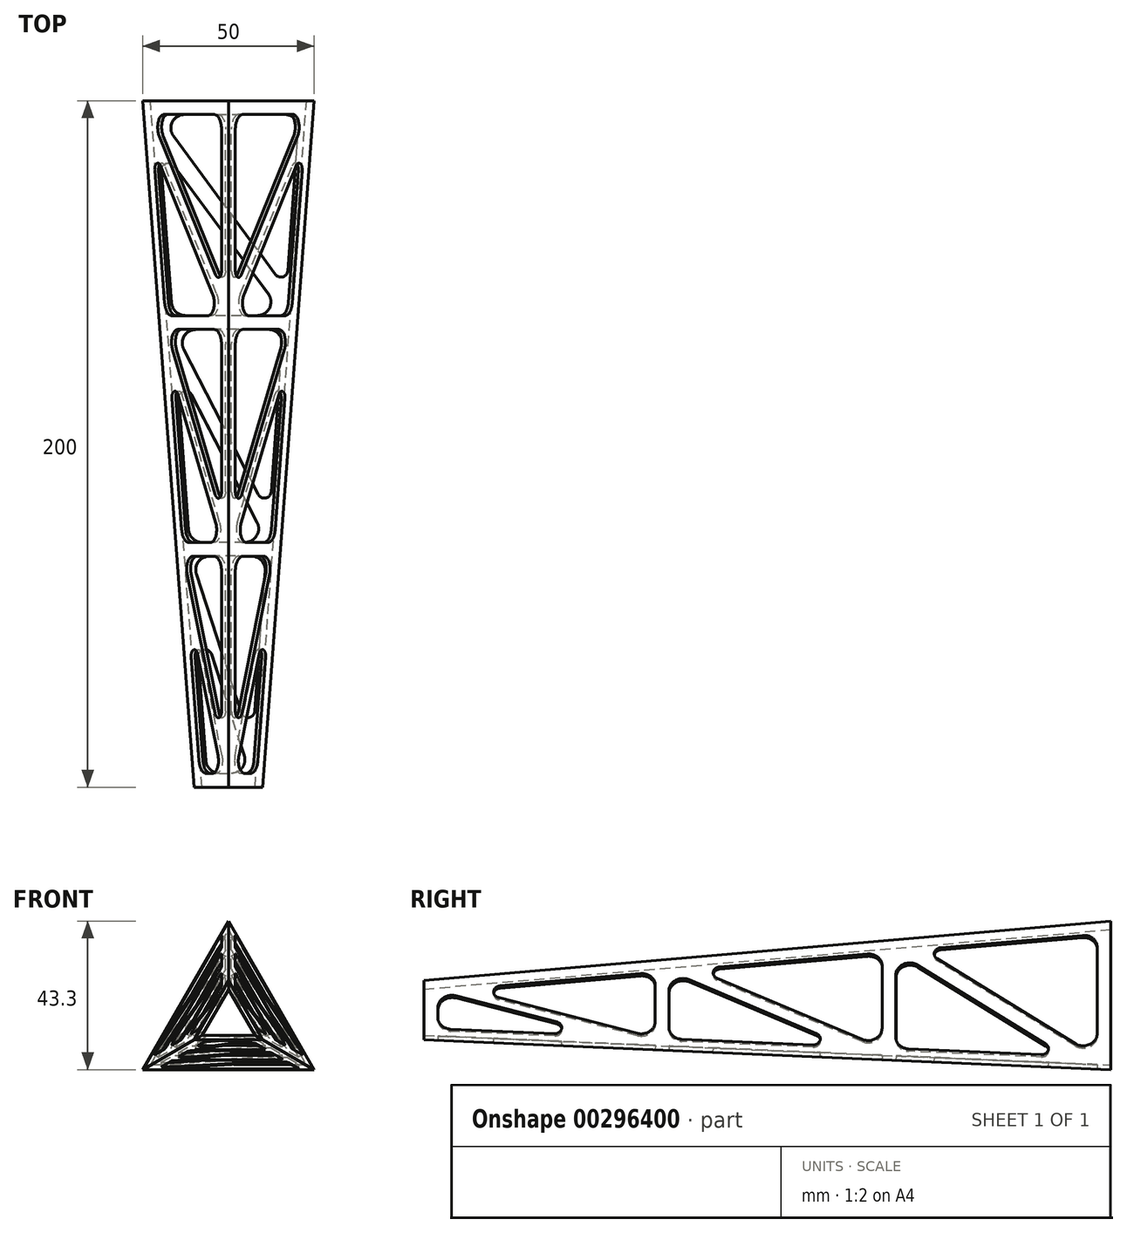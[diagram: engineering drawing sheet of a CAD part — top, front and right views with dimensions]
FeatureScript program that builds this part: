
annotation { "Feature Type Name" : "Feature", "Feature Type Description" : "" }
export const myFeature = defineFeature(function(context is Context, id is Id, definition is map)
    precondition{}
    {
        {
            assignVariable(context, id + "F0", {"name" : "thick", "anyValue" : 4});
        }
        {
            assignVariable(context, id + "F1", {"name" : "thinBy", "anyValue" : 1});
        }
        {
            assignVariable(context, id + "F2", {"name" : "length", "anyValue" : 200});
        }
        {
            assignVariable(context, id + "F3", {"name" : "rad", "anyValue" : 4});
        }
        {
            assignVariable(context, id + "F4", {"name" : "radSmall", "anyValue" : 2});
        }
        {
            var Q0;
            Q0=qCreatedBy(makeId("Right.planeOp"),FACE);
            var sketch = newSketch(context, id + "F5", { "sketchPlane" : qUnion([Q0])});
            skLineSegment(sketch, "E0", {"start": v(0, 0) * mm, "end": v(-200, 0) * mm, "construction": true});
            skSolve(sketch);
        }
        {
            var Q0;
            Q0=qCreatedBy(makeId("Front.planeOp"),FACE);
            var sketch = newSketch(context, id + "F6", { "sketchPlane" : qUnion([Q0])});
            skLineSegment(sketch, "E1", {"start": v(25, -14.43) * mm, "end": v(0, 28.87) * mm});
            skLineSegment(sketch, "E2", {"start": v(25, -14.43) * mm, "end": v(-25, -14.43) * mm});
            skLineSegment(sketch, "E3", {"start": v(0, 28.87) * mm, "end": v(-25, -14.43) * mm});
            skLineSegment(sketch, "E4", {"start": v(0, 28.87) * mm, "end": v(0, -14.43) * mm, "construction": true});
            skLineSegment(sketch, "E5", {"start": v(12.5, 7.22) * mm, "end": v(-25, -14.43) * mm, "construction": true});
            skPoint(sketch, "E6", {"position": v(0, 0) * mm});
            skSolve(sketch);
        }
        {
            var Q0;
            Q0=makeQuery(id+"F6.imprint","IMPRINT",FACE,{"disambiguationData":[TD([[makeQuery(id+"F6.imprint","IMPRINT",EDGE,{"derivedFrom":sQuery(id+"F6.wireOp",EDGE,"E1")}),1.0]])]});
            cPlane(context, id + "F7", {"entities" : qUnion([Q0]), "cplaneType" : CPlaneType.OFFSET, "offset" : (getVariable(context, 'length')) * mm, "width" : 150 * mm, "height" : 150 * mm});
        }
        {
            var Q0;
            Q0=qCreatedBy(id+"F7.planeOp",FACE);
            var sketch = newSketch(context, id + "F8", { "sketchPlane" : qUnion([Q0])});
            skPoint(sketch, "E7.0", {"position": v(0, 28.87) * mm});
            skLineSegment(sketch, "E8.0", {"start": v(25, -14.43) * mm, "end": v(-25, -14.43) * mm, "construction": true});
            skLineSegment(sketch, "E9", {"start": v(0, 11.55) * mm, "end": v(-10, -5.77) * mm});
            skLineSegment(sketch, "E10", {"start": v(-10, -5.77) * mm, "end": v(10, -5.77) * mm});
            skLineSegment(sketch, "E11", {"start": v(10, -5.77) * mm, "end": v(0, 11.55) * mm});
            skLineSegment(sketch, "E12.0", {"start": v(0, 28.87) * mm, "end": v(-25, -14.43) * mm, "construction": true});
            skLineSegment(sketch, "E13.0", {"start": v(25, -14.43) * mm, "end": v(0, 28.87) * mm, "construction": true});
            skLineSegment(sketch, "E14", {"start": v(12.5, 7.22) * mm, "end": v(5, 2.89) * mm, "construction": true});
            skSolve(sketch);
        }
        {
            var Q0;
            Q0=sQuery(id+"F8.wireOp",EDGE,"E11");
            cPoint(context, id + "F9", {"entities" : qUnion([Q0]), "parameter" : 0.5});
        }
        {
            var Q0;
            Q0=sQuery(id+"F6.wireOp",VERTEX,"E4.start");
            var Q1;
            Q1=sQuery(id+"F6.wireOp",VERTEX,"E1.start");
            var Q2;
            Q2 = qCreatedBy(id + "F9" ,VERTEX);
            cPlane(context, id + "F10", {"entities" : qUnion([Q0, Q1, Q2]), "cplaneType" : CPlaneType.THREE_POINT, "offset" : 25 * mm, "width" : 150 * mm, "height" : 150 * mm});
        }
        {
            var Q0;
            Q0=qCreatedBy(id+"F10.planeOp",FACE);
            var sketch = newSketch(context, id + "F11", { "sketchPlane" : qUnion([Q0])});
            skLineSegment(sketch, "E15.0", {"start": v(0.62, -25) * mm, "end": v(0.62, 25) * mm});
            skLineSegment(sketch, "E16.0", {"start": v(-199.56, -10) * mm, "end": v(-199.56, 10) * mm});
            skLineSegment(sketch, "E17", {"start": v(-199.56, 10) * mm, "end": v(0.62, 25) * mm});
            skLineSegment(sketch, "E18", {"start": v(0.62, -25) * mm, "end": v(-199.56, -10) * mm});
            skLineSegment(sketch, "E19.0", {"start": v(-195.56, 6.29) * mm, "end": v(-3.38, 20.69) * mm});
            skLineSegment(sketch, "E19.1", {"start": v(-195.56, -6.29) * mm, "end": v(-195.56, 6.29) * mm});
            skLineSegment(sketch, "E19.2", {"start": v(-3.38, -20.69) * mm, "end": v(-195.56, -6.29) * mm});
            skLineSegment(sketch, "E19.3", {"start": v(-3.38, -20.69) * mm, "end": v(-3.38, 20.69) * mm});
            skLineSegment(sketch, "E20", {"start": v(-132.2, 11.04) * mm, "end": v(-132.2, -11.04) * mm});
            skLineSegment(sketch, "E21", {"start": v(-128.2, 11.34) * mm, "end": v(-128.2, -11.34) * mm});
            skLineSegment(sketch, "E22", {"start": v(-66.07, 16) * mm, "end": v(-66.07, -16) * mm});
            skLineSegment(sketch, "E23", {"start": v(-62.07, 16.3) * mm, "end": v(-62.07, -16.3) * mm});
            skLineSegment(sketch, "E24", {"start": v(-195.56, 6.29) * mm, "end": v(-144.9, -10.08) * mm});
            skLineSegment(sketch, "E25", {"start": v(-132.2, -11.04) * mm, "end": v(-187.64, 6.88) * mm});
            skLineSegment(sketch, "E26", {"start": v(-128.2, 11.34) * mm, "end": v(-76.35, -15.22) * mm});
            skLineSegment(sketch, "E27", {"start": v(-66.07, -16) * mm, "end": v(-120.55, 11.9) * mm});
            skLineSegment(sketch, "E28", {"start": v(-62.07, 16.3) * mm, "end": v(-12.77, -19.99) * mm});
            skLineSegment(sketch, "E29", {"start": v(-3.38, -20.69) * mm, "end": v(-54.41, 16.86) * mm});
            skSolve(sketch);
        }
        {
            var Q0;
            Q0=makeQuery(id+"F11.imprint","IMPRINT",FACE,{"disambiguationData":[TD([[makeQuery(id+"F11.imprint","IMPRINT",EDGE,{"derivedFrom":sQuery(id+"F11.wireOp",EDGE,"E15.0")}),1.0]])]});
            var Q1;
            {var subQ0=sQuery(id+"F11.wireOp",EDGE,"E24");Q1=makeQuery(id+"F11.imprint","IMPRINT",FACE,{"disambiguationData":[TD([[makeQuery(id+"F11.imprint","IMPRINT",EDGE,{"derivedFrom":subQ0}),1.0]])]});}
            var Q2;
            {var subQ0=sQuery(id+"F11.wireOp",EDGE,"E20");Q2=makeQuery(id+"F11.imprint","IMPRINT",FACE,{"disambiguationData":[TD([[makeQuery(id+"F11.imprint","IMPRINT",EDGE,{"derivedFrom":subQ0}),1.0]])]});}
            var Q3;
            {var subQ0=sQuery(id+"F11.wireOp",EDGE,"E26");Q3=makeQuery(id+"F11.imprint","IMPRINT",FACE,{"disambiguationData":[TD([[makeQuery(id+"F11.imprint","IMPRINT",EDGE,{"derivedFrom":subQ0}),1.0]])]});}
            var Q4;
            {var subQ0=sQuery(id+"F11.wireOp",EDGE,"E22");Q4=makeQuery(id+"F11.imprint","IMPRINT",FACE,{"disambiguationData":[TD([[makeQuery(id+"F11.imprint","IMPRINT",EDGE,{"derivedFrom":subQ0}),1.0]])]});}
            var Q5;
            {var subQ0=sQuery(id+"F11.wireOp",EDGE,"E28");Q5=makeQuery(id+"F11.imprint","IMPRINT",FACE,{"disambiguationData":[TD([[makeQuery(id+"F11.imprint","IMPRINT",EDGE,{"derivedFrom":subQ0}),1.0]])]});}
            extrude(context, id + "F12", {"entities" : qUnion([Q0, Q1, Q2, Q3, Q4, Q5]), "oppositeDirection" : true, "depth" : ((getVariable(context, 'thick') / sqrt(3)) - getVariable(context, 'thinBy')) * mm});
        }
        {
            var Q0;
            Q0=makeQuery(id+"F12.opExtrude","SWEPT_EDGE",EDGE,{"disambiguationData":[OSD([sQuery(id+"F11.wireOp",EDGE,"E19.1"),sQuery(id+"F11.wireOp",EDGE,"E19.2")])]});
            var Q1;
            Q1=makeQuery(id+"F12.opExtrude","SWEPT_EDGE",EDGE,{"disambiguationData":[OSD([sQuery(id+"F11.wireOp",EDGE,"E19.2"),sQuery(id+"F11.wireOp",EDGE,"E20"),sQuery(id+"F11.wireOp",EDGE,"E25")])]});
            var Q2;
            Q2=makeQuery(id+"F12.opExtrude","SWEPT_EDGE",EDGE,{"disambiguationData":[OSD([sQuery(id+"F11.wireOp",EDGE,"E19.2"),sQuery(id+"F11.wireOp",EDGE,"E21")])]});
            var Q3;
            Q3=makeQuery(id+"F12.opExtrude","SWEPT_EDGE",EDGE,{"disambiguationData":[OSD([sQuery(id+"F11.wireOp",EDGE,"E19.2"),sQuery(id+"F11.wireOp",EDGE,"E19.3"),sQuery(id+"F11.wireOp",EDGE,"E29")])]});
            var Q4;
            Q4=makeQuery(id+"F12.opExtrude","SWEPT_EDGE",EDGE,{"disambiguationData":[OSD([sQuery(id+"F11.wireOp",EDGE,"E19.0"),sQuery(id+"F11.wireOp",EDGE,"E19.3")])]});
            var Q5;
            Q5=makeQuery(id+"F12.opExtrude","SWEPT_EDGE",EDGE,{"disambiguationData":[OSD([sQuery(id+"F11.wireOp",EDGE,"E19.0"),sQuery(id+"F11.wireOp",EDGE,"E22")])]});
            var Q6;
            Q6=makeQuery(id+"F12.opExtrude","SWEPT_EDGE",EDGE,{"disambiguationData":[OSD([sQuery(id+"F11.wireOp",EDGE,"E19.0"),sQuery(id+"F11.wireOp",EDGE,"E23"),sQuery(id+"F11.wireOp",EDGE,"E28")])]});
            var Q7;
            Q7=makeQuery(id+"F12.opExtrude","SWEPT_EDGE",EDGE,{"disambiguationData":[OSD([sQuery(id+"F11.wireOp",EDGE,"E19.0"),sQuery(id+"F11.wireOp",EDGE,"E19.1"),sQuery(id+"F11.wireOp",EDGE,"E24")])]});
            var Q8;
            Q8=makeQuery(id+"F12.opExtrude","SWEPT_EDGE",EDGE,{"disambiguationData":[OSD([sQuery(id+"F11.wireOp",EDGE,"E19.0"),sQuery(id+"F11.wireOp",EDGE,"E20")])]});
            var Q9;
            Q9=makeQuery(id+"F12.opExtrude","SWEPT_EDGE",EDGE,{"disambiguationData":[OSD([sQuery(id+"F11.wireOp",EDGE,"E19.0"),sQuery(id+"F11.wireOp",EDGE,"E21"),sQuery(id+"F11.wireOp",EDGE,"E26")])]});
            var Q10;
            Q10=makeQuery(id+"F12.opExtrude","SWEPT_EDGE",EDGE,{"disambiguationData":[OSD([sQuery(id+"F11.wireOp",EDGE,"E19.2"),sQuery(id+"F11.wireOp",EDGE,"E22"),sQuery(id+"F11.wireOp",EDGE,"E27")])]});
            var Q11;
            Q11=makeQuery(id+"F12.opExtrude","SWEPT_EDGE",EDGE,{"disambiguationData":[OSD([sQuery(id+"F11.wireOp",EDGE,"E19.2"),sQuery(id+"F11.wireOp",EDGE,"E23")])]});
            fillet(context, id + "F13", {"entities" : qUnion([Q0, Q1, Q2, Q3, Q4, Q5, Q6, Q7, Q8, Q9, Q10, Q11]), "radius" : (getVariable(context, 'rad')) * mm, "tangentPropagation" : true, "allowEdgeOverflow" : false});
        }
        {
            var Q0;
            Q0=makeQuery(id+"F12.opExtrude","SWEPT_EDGE",EDGE,{"disambiguationData":[OSD([sQuery(id+"F11.wireOp",EDGE,"E19.0"),sQuery(id+"F11.wireOp",EDGE,"E27")])]});
            var Q1;
            Q1=makeQuery(id+"F12.opExtrude","SWEPT_EDGE",EDGE,{"disambiguationData":[OSD([sQuery(id+"F11.wireOp",EDGE,"E19.0"),sQuery(id+"F11.wireOp",EDGE,"E25")])]});
            var Q2;
            Q2=makeQuery(id+"F12.opExtrude","SWEPT_EDGE",EDGE,{"disambiguationData":[OSD([sQuery(id+"F11.wireOp",EDGE,"E19.2"),sQuery(id+"F11.wireOp",EDGE,"E24")])]});
            var Q3;
            Q3=makeQuery(id+"F12.opExtrude","SWEPT_EDGE",EDGE,{"disambiguationData":[OSD([sQuery(id+"F11.wireOp",EDGE,"E19.2"),sQuery(id+"F11.wireOp",EDGE,"E26")])]});
            var Q4;
            Q4=makeQuery(id+"F12.opExtrude","SWEPT_EDGE",EDGE,{"disambiguationData":[OSD([sQuery(id+"F11.wireOp",EDGE,"E19.0"),sQuery(id+"F11.wireOp",EDGE,"E29")])]});
            var Q5;
            Q5=makeQuery(id+"F12.opExtrude","SWEPT_EDGE",EDGE,{"disambiguationData":[OSD([sQuery(id+"F11.wireOp",EDGE,"E19.2"),sQuery(id+"F11.wireOp",EDGE,"E28")])]});
            fillet(context, id + "F14", {"entities" : qUnion([Q0, Q1, Q2, Q3, Q4, Q5]), "radius" : (getVariable(context, 'radSmall')) * mm, "tangentPropagation" : true, "allowEdgeOverflow" : false});
        }
        {
            var Q0;
            Q0=makeQuery(id+"F12.opExtrude","SWEPT_BODY",BODY,{"disambiguationData":[OSD([sQuery(id+"F11.wireOp",EDGE,"E15.0"),sQuery(id+"F11.wireOp",EDGE,"E16.0"),sQuery(id+"F11.wireOp",EDGE,"E17"),sQuery(id+"F11.wireOp",EDGE,"E18"),sQuery(id+"F11.wireOp",EDGE,"E19.0"),sQuery(id+"F11.wireOp",EDGE,"E19.1"),sQuery(id+"F11.wireOp",EDGE,"E19.2"),sQuery(id+"F11.wireOp",EDGE,"E19.3"),sQuery(id+"F11.wireOp",EDGE,"E20"),sQuery(id+"F11.wireOp",EDGE,"E21"),sQuery(id+"F11.wireOp",EDGE,"E22"),sQuery(id+"F11.wireOp",EDGE,"E23"),sQuery(id+"F11.wireOp",EDGE,"E24"),sQuery(id+"F11.wireOp",EDGE,"E25"),sQuery(id+"F11.wireOp",EDGE,"E26"),sQuery(id+"F11.wireOp",EDGE,"E27"),sQuery(id+"F11.wireOp",EDGE,"E28"),sQuery(id+"F11.wireOp",EDGE,"E29")])]});
            var Q1;
            Q1=sQuery(id+"F5.wireOp",EDGE,"E0");
            circularPattern(context, id + "F15", {"entities" : qUnion([Q0]), "axis" : qUnion([Q1]), "angle" : 360 * degree, "instanceCount" : 3, "equalSpace" : true});
        }
        {
            var Q0;
            Q0=makeQuery(id+"F15.opPattern","COPY",BODY,{"derivedFrom":makeQuery(id+"F12.opExtrude","SWEPT_BODY",BODY,{"disambiguationData":[OSD([sQuery(id+"F11.wireOp",EDGE,"E15.0"),sQuery(id+"F11.wireOp",EDGE,"E16.0"),sQuery(id+"F11.wireOp",EDGE,"E17"),sQuery(id+"F11.wireOp",EDGE,"E18"),sQuery(id+"F11.wireOp",EDGE,"E19.0"),sQuery(id+"F11.wireOp",EDGE,"E19.1"),sQuery(id+"F11.wireOp",EDGE,"E19.2"),sQuery(id+"F11.wireOp",EDGE,"E19.3"),sQuery(id+"F11.wireOp",EDGE,"E20"),sQuery(id+"F11.wireOp",EDGE,"E21"),sQuery(id+"F11.wireOp",EDGE,"E22"),sQuery(id+"F11.wireOp",EDGE,"E23"),sQuery(id+"F11.wireOp",EDGE,"E24"),sQuery(id+"F11.wireOp",EDGE,"E25"),sQuery(id+"F11.wireOp",EDGE,"E26"),sQuery(id+"F11.wireOp",EDGE,"E27"),sQuery(id+"F11.wireOp",EDGE,"E28"),sQuery(id+"F11.wireOp",EDGE,"E29")])]}),"instanceName":"1"});
            deleteBodies(context, id + "F16", {"entities" : qUnion([Q0])});
        }
        {
            var Q0;
            Q0=makeQuery(id+"F12.opExtrude","SWEPT_BODY",BODY,{"disambiguationData":[OSD([sQuery(id+"F11.wireOp",EDGE,"E15.0"),sQuery(id+"F11.wireOp",EDGE,"E16.0"),sQuery(id+"F11.wireOp",EDGE,"E17"),sQuery(id+"F11.wireOp",EDGE,"E18"),sQuery(id+"F11.wireOp",EDGE,"E19.0"),sQuery(id+"F11.wireOp",EDGE,"E19.1"),sQuery(id+"F11.wireOp",EDGE,"E19.2"),sQuery(id+"F11.wireOp",EDGE,"E19.3"),sQuery(id+"F11.wireOp",EDGE,"E20"),sQuery(id+"F11.wireOp",EDGE,"E21"),sQuery(id+"F11.wireOp",EDGE,"E22"),sQuery(id+"F11.wireOp",EDGE,"E23"),sQuery(id+"F11.wireOp",EDGE,"E24"),sQuery(id+"F11.wireOp",EDGE,"E25"),sQuery(id+"F11.wireOp",EDGE,"E26"),sQuery(id+"F11.wireOp",EDGE,"E27"),sQuery(id+"F11.wireOp",EDGE,"E28"),sQuery(id+"F11.wireOp",EDGE,"E29")])]});
            var Q1;
            Q1=qCreatedBy(makeId("Right.planeOp"),FACE);
            mirror(context, id + "F17", {"entities" : qUnion([Q0]), "mirrorPlane" : qUnion([Q1])});
        }
        {
            var Q1;
            Q1=makeQuery(id+"F6.imprint","IMPRINT",FACE,{"disambiguationData":[TD([[makeQuery(id+"F6.imprint","IMPRINT",EDGE,{"derivedFrom":sQuery(id+"F6.wireOp",EDGE,"E1")}),1.0]])]});
            var Q2;
            Q2=makeQuery(id+"F8.imprint","IMPRINT",FACE,{"disambiguationData":[TD([[makeQuery(id+"F8.imprint","IMPRINT",EDGE,{"derivedFrom":sQuery(id+"F8.wireOp",EDGE,"E9")}),1.0]])]});
            loft(context, id + "F18", {"operationType" : NewBodyOperationType.INTERSECT, "sheetProfilesArray" : [{ "sheetProfileEntities" : qUnion([Q1]) }, { "sheetProfileEntities" : qUnion([Q2]) }]});
        }
        {
            var Q0;
            Q0=makeQuery(id+"F12.opExtrude","SWEPT_BODY",BODY,{"disambiguationData":[OSD([sQuery(id+"F11.wireOp",EDGE,"E15.0"),sQuery(id+"F11.wireOp",EDGE,"E16.0"),sQuery(id+"F11.wireOp",EDGE,"E17"),sQuery(id+"F11.wireOp",EDGE,"E18"),sQuery(id+"F11.wireOp",EDGE,"E19.0"),sQuery(id+"F11.wireOp",EDGE,"E19.1"),sQuery(id+"F11.wireOp",EDGE,"E19.2"),sQuery(id+"F11.wireOp",EDGE,"E19.3"),sQuery(id+"F11.wireOp",EDGE,"E20"),sQuery(id+"F11.wireOp",EDGE,"E21"),sQuery(id+"F11.wireOp",EDGE,"E22"),sQuery(id+"F11.wireOp",EDGE,"E23"),sQuery(id+"F11.wireOp",EDGE,"E24"),sQuery(id+"F11.wireOp",EDGE,"E25"),sQuery(id+"F11.wireOp",EDGE,"E26"),sQuery(id+"F11.wireOp",EDGE,"E27"),sQuery(id+"F11.wireOp",EDGE,"E28"),sQuery(id+"F11.wireOp",EDGE,"E29")])]});
            var Q1;
            Q1=makeQuery(id+"F15.opPattern","COPY",BODY,{"derivedFrom":makeQuery(id+"F12.opExtrude","SWEPT_BODY",BODY,{"disambiguationData":[OSD([sQuery(id+"F11.wireOp",EDGE,"E15.0"),sQuery(id+"F11.wireOp",EDGE,"E16.0"),sQuery(id+"F11.wireOp",EDGE,"E17"),sQuery(id+"F11.wireOp",EDGE,"E18"),sQuery(id+"F11.wireOp",EDGE,"E19.0"),sQuery(id+"F11.wireOp",EDGE,"E19.1"),sQuery(id+"F11.wireOp",EDGE,"E19.2"),sQuery(id+"F11.wireOp",EDGE,"E19.3"),sQuery(id+"F11.wireOp",EDGE,"E20"),sQuery(id+"F11.wireOp",EDGE,"E21"),sQuery(id+"F11.wireOp",EDGE,"E22"),sQuery(id+"F11.wireOp",EDGE,"E23"),sQuery(id+"F11.wireOp",EDGE,"E24"),sQuery(id+"F11.wireOp",EDGE,"E25"),sQuery(id+"F11.wireOp",EDGE,"E26"),sQuery(id+"F11.wireOp",EDGE,"E27"),sQuery(id+"F11.wireOp",EDGE,"E28"),sQuery(id+"F11.wireOp",EDGE,"E29")])]}),"instanceName":"2"});
            var Q2;
            Q2=makeQuery(id+"F17.opPattern","COPY",BODY,{"derivedFrom":makeQuery(id+"F12.opExtrude","SWEPT_BODY",BODY,{"disambiguationData":[OSD([sQuery(id+"F11.wireOp",EDGE,"E15.0"),sQuery(id+"F11.wireOp",EDGE,"E16.0"),sQuery(id+"F11.wireOp",EDGE,"E17"),sQuery(id+"F11.wireOp",EDGE,"E18"),sQuery(id+"F11.wireOp",EDGE,"E19.0"),sQuery(id+"F11.wireOp",EDGE,"E19.1"),sQuery(id+"F11.wireOp",EDGE,"E19.2"),sQuery(id+"F11.wireOp",EDGE,"E19.3"),sQuery(id+"F11.wireOp",EDGE,"E20"),sQuery(id+"F11.wireOp",EDGE,"E21"),sQuery(id+"F11.wireOp",EDGE,"E22"),sQuery(id+"F11.wireOp",EDGE,"E23"),sQuery(id+"F11.wireOp",EDGE,"E24"),sQuery(id+"F11.wireOp",EDGE,"E25"),sQuery(id+"F11.wireOp",EDGE,"E26"),sQuery(id+"F11.wireOp",EDGE,"E27"),sQuery(id+"F11.wireOp",EDGE,"E28"),sQuery(id+"F11.wireOp",EDGE,"E29")])]}),"instanceName":"1"});
            booleanBodies(context, id + "F19", {"operationType" : BooleanOperationType.UNION, "tools" : qUnion([Q0, Q1, Q2])});
        }
    });
